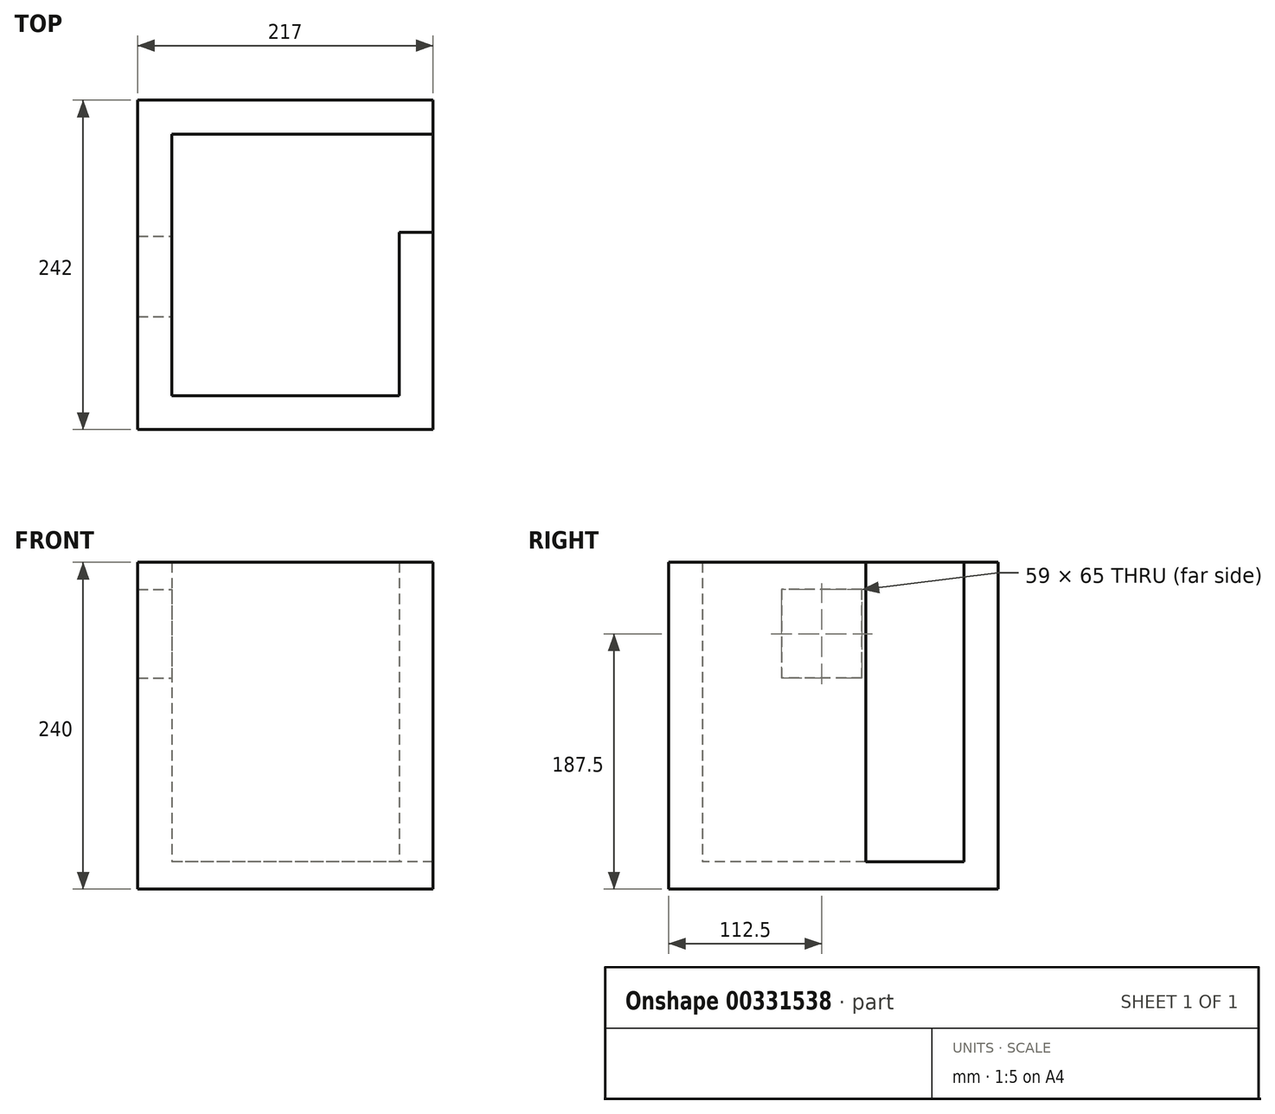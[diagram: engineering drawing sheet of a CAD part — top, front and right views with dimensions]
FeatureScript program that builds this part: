
annotation { "Feature Type Name" : "Feature", "Feature Type Description" : "" }
export const myFeature = defineFeature(function(context is Context, id is Id, definition is map)
    precondition{}
    {
        {
            var Q0;
            Q0=qCreatedBy(makeId("Top.planeOp"),FACE);
            var sketch = newSketch(context, id + "F0", { "sketchPlane" : qUnion([Q0])});
            skLineSegment(sketch, "E0", {"start": v(1313, 440) * mm, "end": v(1313, 406) * mm});
            skLineSegment(sketch, "E1", {"start": v(1313, -267) * mm, "end": v(1313, -301) * mm});
            skLineSegment(sketch, "E2", {"start": v(1313, -301) * mm, "end": v(647, -301) * mm});
            skLineSegment(sketch, "E3", {"start": v(1279, -267) * mm, "end": v(647, -267) * mm});
            skLineSegment(sketch, "E4", {"start": v(1279, 406) * mm, "end": v(688, 406) * mm});
            skLineSegment(sketch, "E5", {"start": v(688, 406) * mm, "end": v(688, -75) * mm});
            skLineSegment(sketch, "E6", {"start": v(688, -75) * mm, "end": v(413, -75) * mm});
            skLineSegment(sketch, "E7", {"start": v(647, -301) * mm, "end": v(647, -267) * mm});
            skLineSegment(sketch, "E8", {"start": v(536, -301) * mm, "end": v(536, -267) * mm});
            skLineSegment(sketch, "E9", {"start": v(536, -267) * mm, "end": v(328, -267) * mm});
            skLineSegment(sketch, "E10", {"start": v(328, -267) * mm, "end": v(328, -407) * mm});
            skLineSegment(sketch, "E11", {"start": v(328, -407) * mm, "end": v(-40, -407) * mm});
            skLineSegment(sketch, "E12", {"start": v(-40, -407) * mm, "end": v(-40, -188) * mm});
            skLineSegment(sketch, "E13", {"start": v(-40, -188) * mm, "end": v(-105, -188) * mm});
            skLineSegment(sketch, "E14", {"start": v(536, -301) * mm, "end": v(362, -301) * mm});
            skLineSegment(sketch, "E15", {"start": v(362, -301) * mm, "end": v(362, -440) * mm});
            skLineSegment(sketch, "E16", {"start": v(-60, -407) * mm, "end": v(-60, -215) * mm});
            skLineSegment(sketch, "E17", {"start": v(-60, -215) * mm, "end": v(-105, -215) * mm});
            skLineSegment(sketch, "E18", {"start": v(-105, -188) * mm, "end": v(-105, -215) * mm});
            skLineSegment(sketch, "E19", {"start": v(-60, -407) * mm, "end": v(-282, -407) * mm});
            skLineSegment(sketch, "E20", {"start": v(-282, -407) * mm, "end": v(-282, -287) * mm});
            skLineSegment(sketch, "E21", {"start": v(-282, -287) * mm, "end": v(-330, -287) * mm});
            skLineSegment(sketch, "E22", {"start": v(-330, -287) * mm, "end": v(-330, -407) * mm});
            skLineSegment(sketch, "E23", {"start": v(-330, -407) * mm, "end": v(-497, -407) * mm});
            skLineSegment(sketch, "E24", {"start": v(-197, -188) * mm, "end": v(-197, -215) * mm});
            skLineSegment(sketch, "E25", {"start": v(-197, -188) * mm, "end": v(-765, -188) * mm});
            skLineSegment(sketch, "E26", {"start": v(-197, -215) * mm, "end": v(-497, -215) * mm});
            skLineSegment(sketch, "E27", {"start": v(-497, -215) * mm, "end": v(-497, -231) * mm});
            skLineSegment(sketch, "E28", {"start": v(-497, -231) * mm, "end": v(-497, -293) * mm});
            skLineSegment(sketch, "E29", {"start": v(-497, -407) * mm, "end": v(-497, -349) * mm});
            skLineSegment(sketch, "E30", {"start": v(413, -75) * mm, "end": v(413, -54) * mm});
            skLineSegment(sketch, "E31", {"start": v(413, -54) * mm, "end": v(667, -54) * mm});
            skLineSegment(sketch, "E32", {"start": v(667, -54) * mm, "end": v(667, 406) * mm});
            skLineSegment(sketch, "E33", {"start": v(667, 406) * mm, "end": v(495, 406) * mm});
            skLineSegment(sketch, "E34", {"start": v(312, 406) * mm, "end": v(391, 406) * mm});
            skLineSegment(sketch, "E35", {"start": v(391, 406) * mm, "end": v(391, 440) * mm});
            skLineSegment(sketch, "E36", {"start": v(495, 406) * mm, "end": v(495, 440) * mm});
            skLineSegment(sketch, "E37", {"start": v(1313, 440) * mm, "end": v(495, 440) * mm});
            skLineSegment(sketch, "E38", {"start": v(312, -75) * mm, "end": v(60, -75) * mm});
            skLineSegment(sketch, "E39", {"start": v(-1279, 406) * mm, "end": v(-1279, 7) * mm});
            skLineSegment(sketch, "E40", {"start": v(-790, 406) * mm, "end": v(-790, 7) * mm});
            skLineSegment(sketch, "E41", {"start": v(-1279, 7) * mm, "end": v(-910, 7) * mm});
            skLineSegment(sketch, "E42", {"start": v(-790, 7) * mm, "end": v(-808, 7) * mm});
            skLineSegment(sketch, "E43", {"start": v(-765, -188) * mm, "end": v(-765, -208) * mm});
            skLineSegment(sketch, "E44", {"start": v(290, 141) * mm, "end": v(290, 406) * mm});
            skLineSegment(sketch, "E45", {"start": v(290, 141) * mm, "end": v(75, 141) * mm});
            skLineSegment(sketch, "E46", {"start": v(75, -46) * mm, "end": v(75, 141) * mm});
            skLineSegment(sketch, "E47", {"start": v(60, -75) * mm, "end": v(60, -46) * mm});
            skLineSegment(sketch, "E48", {"start": v(391, 406) * mm, "end": v(312, 406) * mm});
            skLineSegment(sketch, "E49", {"start": v(-139, 406) * mm, "end": v(-139, 440) * mm});
            skLineSegment(sketch, "E50", {"start": v(-318, 406) * mm, "end": v(-318, 440) * mm});
            skLineSegment(sketch, "E51", {"start": v(-515, 406) * mm, "end": v(-515, 440) * mm});
            skLineSegment(sketch, "E52", {"start": v(-694, 406) * mm, "end": v(-694, 440) * mm});
            skLineSegment(sketch, "E53", {"start": v(-770, 406) * mm, "end": v(-770, 9) * mm});
            skLineSegment(sketch, "E54", {"start": v(-694, 406) * mm, "end": v(-770, 406) * mm});
            skLineSegment(sketch, "E55", {"start": v(75, 406) * mm, "end": v(-139, 406) * mm});
            skLineSegment(sketch, "E56", {"start": v(-318, 406) * mm, "end": v(-515, 406) * mm});
            skLineSegment(sketch, "E57", {"start": v(-318, 440) * mm, "end": v(-515, 440) * mm});
            skLineSegment(sketch, "E58", {"start": v(-770, 9) * mm, "end": v(-754, 9) * mm});
            skLineSegment(sketch, "E59", {"start": v(-677, 9) * mm, "end": v(-659, 9) * mm});
            skLineSegment(sketch, "E60", {"start": v(-659, 9) * mm, "end": v(-659, -5) * mm});
            skLineSegment(sketch, "E61", {"start": v(-659, -5) * mm, "end": v(-659, -46) * mm});
            skLineSegment(sketch, "E62", {"start": v(-659, -46) * mm, "end": v(-60, -46) * mm});
            skLineSegment(sketch, "E63", {"start": v(-60, -75) * mm, "end": v(-60, -46) * mm});
            skLineSegment(sketch, "E64", {"start": v(60, -75) * mm, "end": v(128, -75) * mm});
            skLineSegment(sketch, "E65", {"start": v(60, -46) * mm, "end": v(75, -46) * mm});
            skLineSegment(sketch, "E66", {"start": v(96, -46) * mm, "end": v(290, -46) * mm});
            skLineSegment(sketch, "E67", {"start": v(-60, -75) * mm, "end": v(-677, -75) * mm});
            skLineSegment(sketch, "E68", {"start": v(-677, 9) * mm, "end": v(-677, -75) * mm});
            skLineSegment(sketch, "E69", {"start": v(-754, 9) * mm, "end": v(-754, -13) * mm});
            skLineSegment(sketch, "E70", {"start": v(-808, 7) * mm, "end": v(-808, -13) * mm});
            skLineSegment(sketch, "E71", {"start": v(-808, -13) * mm, "end": v(-754, -13) * mm});
            skLineSegment(sketch, "E72", {"start": v(-910, 7) * mm, "end": v(-910, -29) * mm});
            skLineSegment(sketch, "E73", {"start": v(-1279, -406) * mm, "end": v(-935, -406) * mm});
            skLineSegment(sketch, "E74", {"start": v(-1313, -440) * mm, "end": v(-935, -440) * mm});
            skLineSegment(sketch, "E75", {"start": v(-910, -29) * mm, "end": v(-935, -29) * mm});
            skLineSegment(sketch, "E76", {"start": v(-935, -13) * mm, "end": v(-1279, -13) * mm});
            skLineSegment(sketch, "E77", {"start": v(-910, -132) * mm, "end": v(-935, -132) * mm});
            skLineSegment(sketch, "E78", {"start": v(-910, -29) * mm, "end": v(-910, -13) * mm});
            skLineSegment(sketch, "E79", {"start": v(-935, -406) * mm, "end": v(-935, -132) * mm});
            skLineSegment(sketch, "E80", {"start": v(-935, -29) * mm, "end": v(-935, -13) * mm});
            skLineSegment(sketch, "E81", {"start": v(-877, -208) * mm, "end": v(-877, -188) * mm});
            skLineSegment(sketch, "E82", {"start": v(-910, -132) * mm, "end": v(-910, -188) * mm});
            skLineSegment(sketch, "E83", {"start": v(-877, -188) * mm, "end": v(-910, -188) * mm});
            skLineSegment(sketch, "E84", {"start": v(-877, -208) * mm, "end": v(-904, -208) * mm});
            skLineSegment(sketch, "E85", {"start": v(-904, -208) * mm, "end": v(-904, -406) * mm});
            skLineSegment(sketch, "E86", {"start": v(-904, -406) * mm, "end": v(-648, -406) * mm});
            skLineSegment(sketch, "E87", {"start": v(-765, -208) * mm, "end": v(-648, -208) * mm});
            skLineSegment(sketch, "E88", {"start": v(-648, -208) * mm, "end": v(-648, -273) * mm});
            skLineSegment(sketch, "E89", {"start": v(-648, -406) * mm, "end": v(-648, -343) * mm});
            skLineSegment(sketch, "E90", {"start": v(-935, -440) * mm, "end": v(362, -440) * mm});
            skLineSegment(sketch, "E91", {"start": v(151, 406) * mm, "end": v(151, 440) * mm});
            skLineSegment(sketch, "E92", {"start": v(224, 406) * mm, "end": v(224, 440) * mm});
            skLineSegment(sketch, "E93", {"start": v(290, 406) * mm, "end": v(224, 406) * mm});
            skLineSegment(sketch, "E94", {"start": v(151, 406) * mm, "end": v(96, 406) * mm});
            skLineSegment(sketch, "E95", {"start": v(391, 440) * mm, "end": v(224, 440) * mm});
            skLineSegment(sketch, "E96", {"start": v(151, 440) * mm, "end": v(-139, 440) * mm});
            skLineSegment(sketch, "E97", {"start": v(-907, 406) * mm, "end": v(-907, 440) * mm});
            skLineSegment(sketch, "E98", {"start": v(-1085, 406) * mm, "end": v(-1085, 440) * mm});
            skLineSegment(sketch, "E99", {"start": v(-790, 406) * mm, "end": v(-907, 406) * mm});
            skLineSegment(sketch, "E100", {"start": v(-1085, 406) * mm, "end": v(-1279, 406) * mm});
            skLineSegment(sketch, "E101", {"start": v(-694, 440) * mm, "end": v(-907, 440) * mm});
            skLineSegment(sketch, "E102", {"start": v(-1085, 440) * mm, "end": v(-1313, 440) * mm});
            skLineSegment(sketch, "E103", {"start": v(-1279, -118) * mm, "end": v(-1313, -118) * mm});
            skLineSegment(sketch, "E104", {"start": v(-1279, -297) * mm, "end": v(-1313, -297) * mm});
            skLineSegment(sketch, "E105", {"start": v(-1279, -13) * mm, "end": v(-1279, -118) * mm});
            skLineSegment(sketch, "E106", {"start": v(-1279, -297) * mm, "end": v(-1279, -406) * mm});
            skLineSegment(sketch, "E107", {"start": v(-1313, 440) * mm, "end": v(-1313, -118) * mm});
            skLineSegment(sketch, "E108", {"start": v(-1313, -297) * mm, "end": v(-1313, -440) * mm});
            skLineSegment(sketch, "E109", {"start": v(-648, -273) * mm, "end": v(-630, -273) * mm});
            skLineSegment(sketch, "E110", {"start": v(-648, -343) * mm, "end": v(-630, -343) * mm});
            skLineSegment(sketch, "E111", {"start": v(-515, -349) * mm, "end": v(-497, -349) * mm});
            skLineSegment(sketch, "E112", {"start": v(-515, -293) * mm, "end": v(-497, -293) * mm});
            skLineSegment(sketch, "E113", {"start": v(-515, -349) * mm, "end": v(-515, -406) * mm});
            skLineSegment(sketch, "E114", {"start": v(-630, -343) * mm, "end": v(-630, -406) * mm});
            skLineSegment(sketch, "E115", {"start": v(-630, -406) * mm, "end": v(-515, -406) * mm});
            skLineSegment(sketch, "E116", {"start": v(-630, -273) * mm, "end": v(-630, -206) * mm});
            skLineSegment(sketch, "E117", {"start": v(-630, -206) * mm, "end": v(-515, -206) * mm});
            skLineSegment(sketch, "E118", {"start": v(-515, -293) * mm, "end": v(-515, -206) * mm});
            skLineSegment(sketch, "E119", {"start": v(290, 43) * mm, "end": v(312, 43) * mm});
            skLineSegment(sketch, "E120", {"start": v(290, 124) * mm, "end": v(312, 124) * mm});
            skLineSegment(sketch, "E121", {"start": v(312, -75) * mm, "end": v(312, 43) * mm});
            skLineSegment(sketch, "E122", {"start": v(312, 124) * mm, "end": v(312, 406) * mm});
            skLineSegment(sketch, "E123", {"start": v(290, -46) * mm, "end": v(290, 43) * mm});
            skLineSegment(sketch, "E124", {"start": v(96, 222) * mm, "end": v(75, 222) * mm});
            skLineSegment(sketch, "E125", {"start": v(96, 222) * mm, "end": v(96, 406) * mm});
            skLineSegment(sketch, "E126", {"start": v(75, 222) * mm, "end": v(75, 406) * mm});
            skLineSegment(sketch, "E127", {"start": v(96, -46) * mm, "end": v(96, 124) * mm});
            skLineSegment(sketch, "E128", {"start": v(290, 124) * mm, "end": v(96, 124) * mm});
            skLineSegment(sketch, "E129", {"start": v(1279, -219) * mm, "end": v(1313, -219) * mm});
            skLineSegment(sketch, "E130", {"start": v(1279, -26) * mm, "end": v(1313, -26) * mm});
            skLineSegment(sketch, "E131", {"start": v(1279, 46) * mm, "end": v(1313, 46) * mm});
            skLineSegment(sketch, "E132", {"start": v(1279, 239) * mm, "end": v(1313, 239) * mm});
            skLineSegment(sketch, "E133", {"start": v(1313, 406) * mm, "end": v(1313, 239) * mm});
            skLineSegment(sketch, "E134", {"start": v(1279, 406) * mm, "end": v(1279, 239) * mm});
            skLineSegment(sketch, "E135", {"start": v(1313, 46) * mm, "end": v(1313, -26) * mm});
            skLineSegment(sketch, "E136", {"start": v(1313, -219) * mm, "end": v(1313, -267) * mm});
            skLineSegment(sketch, "E137", {"start": v(1279, 46) * mm, "end": v(1279, -26) * mm});
            skLineSegment(sketch, "E138", {"start": v(1279, -219) * mm, "end": v(1279, -267) * mm});
            skLineSegment(sketch, "E139", {"start": v(1313, -301) * mm, "end": v(1313, 440) * mm});
            skLineSegment(sketch, "E140", {"start": v(1313, -301) * mm, "end": v(362, -301) * mm});
            skLineSegment(sketch, "E141", {"start": v(362, -440) * mm, "end": v(-1313, -440) * mm});
            skLineSegment(sketch, "E142", {"start": v(-1313, 440) * mm, "end": v(-1313, -440) * mm});
            skLineSegment(sketch, "E143", {"start": v(-1313, 440) * mm, "end": v(1313, 440) * mm});
            skLineSegment(sketch, "E144", {"start": v(-321.5, -37.21) * mm, "end": v(-321.5, 162.79) * mm});
            skLineSegment(sketch, "E145", {"start": v(-321.5, -37.21) * mm, "end": v(-511.5, -37.21) * mm});
            skLineSegment(sketch, "E146", {"start": v(-321.5, 162.79) * mm, "end": v(-511.5, 162.79) * mm});
            skLineSegment(sketch, "E147", {"start": v(-511.5, -37.21) * mm, "end": v(-511.5, 162.79) * mm});
            skLineSegment(sketch, "E148", {"start": v(-321.5, -29.2) * mm, "end": v(-511.5, -29.2) * mm});
            skLineSegment(sketch, "E149", {"start": v(-499.08, -21.75) * mm, "end": v(-430.85, -21.75) * mm});
            skLineSegment(sketch, "E150", {"start": v(-430.85, -21.75) * mm, "end": v(-430.85, 2.94) * mm});
            skLineSegment(sketch, "E151", {"start": v(-430.85, 2.94) * mm, "end": v(-499.08, 2.94) * mm});
            skLineSegment(sketch, "E152", {"start": v(-499.08, 2.94) * mm, "end": v(-499.08, -21.75) * mm});
            skLineSegment(sketch, "E153", {"start": v(-333.92, -21.75) * mm, "end": v(-402.15, -21.75) * mm});
            skLineSegment(sketch, "E154", {"start": v(-402.15, -21.75) * mm, "end": v(-402.15, 2.94) * mm});
            skLineSegment(sketch, "E155", {"start": v(-402.15, 2.94) * mm, "end": v(-333.92, 2.94) * mm});
            skLineSegment(sketch, "E156", {"start": v(-333.92, 2.94) * mm, "end": v(-333.92, -21.75) * mm});
            skLineSegment(sketch, "E157", {"start": v(-321.5, 13.1) * mm, "end": v(-416.5, 13.1) * mm});
            skLineSegment(sketch, "E158", {"start": v(-511.5, 36.6) * mm, "end": v(-491.94, 63.04) * mm});
            skLineSegment(sketch, "E159", {"start": v(-491.94, 63.04) * mm, "end": v(-416.5, 13.1) * mm});
            skLineSegment(sketch, "E160", {"start": v(-416.5, 13.1) * mm, "end": v(-511.5, 36.6) * mm});
            skLineSegment(sketch, "E161", {"start": v(-321.5, 159.23) * mm, "end": v(-511.5, 159.23) * mm});
            skLineSegment(sketch, "E162", {"start": v(-552.43, 3.31) * mm, "end": v(-520.43, 3.31) * mm});
            skLineSegment(sketch, "E163", {"start": v(-552.43, 3.31) * mm, "end": v(-552.43, -36.7) * mm});
            skLineSegment(sketch, "E164", {"start": v(-520.43, 3.31) * mm, "end": v(-520.43, -36.7) * mm});
            skLineSegment(sketch, "E165", {"start": v(-552.43, -36.7) * mm, "end": v(-520.43, -36.7) * mm});
            skLineSegment(sketch, "E166", {"start": v(-552.43, -6.69) * mm, "end": v(-520.43, -6.69) * mm});
            skLineSegment(sketch, "E167", {"start": v(-552.43, -3.69) * mm, "end": v(-520.43, -3.69) * mm});
            skLineSegment(sketch, "E168", {"start": v(-552.43, -0.69) * mm, "end": v(-520.43, -0.69) * mm});
            skLineSegment(sketch, "E169", {"start": v(-552.43, 2.31) * mm, "end": v(-520.43, 2.31) * mm});
            skLineSegment(sketch, "E170", {"start": v(-280.57, 3.31) * mm, "end": v(-312.57, 3.31) * mm});
            skLineSegment(sketch, "E171", {"start": v(-280.57, 3.31) * mm, "end": v(-280.57, -36.7) * mm});
            skLineSegment(sketch, "E172", {"start": v(-312.57, 3.31) * mm, "end": v(-312.57, -36.7) * mm});
            skLineSegment(sketch, "E173", {"start": v(-280.57, -36.7) * mm, "end": v(-312.57, -36.7) * mm});
            skLineSegment(sketch, "E174", {"start": v(-280.57, -6.69) * mm, "end": v(-312.57, -6.69) * mm});
            skLineSegment(sketch, "E175", {"start": v(-280.57, -3.69) * mm, "end": v(-312.57, -3.69) * mm});
            skLineSegment(sketch, "E176", {"start": v(-280.57, -0.69) * mm, "end": v(-312.57, -0.69) * mm});
            skLineSegment(sketch, "E177", {"start": v(-280.57, 2.31) * mm, "end": v(-312.57, 2.31) * mm});
            skLineSegment(sketch, "E178", {"start": v(-765, 395.6) * mm, "end": v(-765, 20.6) * mm});
            skLineSegment(sketch, "E179", {"start": v(-765, 395.6) * mm, "end": v(-705, 395.6) * mm});
            skLineSegment(sketch, "E180", {"start": v(-705, 395.6) * mm, "end": v(-705, 20.6) * mm});
            skLineSegment(sketch, "E181", {"start": v(-765, 20.6) * mm, "end": v(-705, 20.6) * mm});
            skLineSegment(sketch, "E182", {"start": v(-705, 395.6) * mm, "end": v(-700, 395.6) * mm});
            skLineSegment(sketch, "E183", {"start": v(-700, 395.6) * mm, "end": v(-700, 20.6) * mm});
            skLineSegment(sketch, "E184", {"start": v(-705, 20.6) * mm, "end": v(-700, 20.6) * mm});
            skLineSegment(sketch, "E185", {"start": v(-705, 114.35) * mm, "end": v(-700, 114.35) * mm});
            skLineSegment(sketch, "E186", {"start": v(-705, 301.85) * mm, "end": v(-700, 301.85) * mm});
            skLineSegment(sketch, "E187", {"start": v(-705, 208.1) * mm, "end": v(-700, 208.1) * mm});
            skLineSegment(sketch, "E188", {"start": v(-705, 348.73) * mm, "end": v(-700, 348.73) * mm});
            skLineSegment(sketch, "E189", {"start": v(-705, 67.47) * mm, "end": v(-700, 67.47) * mm});
            skSolve(sketch);
        }
        {
            var Q0;
            Q0=makeQuery(id+"F0.imprint","IMPRINT",FACE,{"disambiguationData":[TD([[makeQuery(id+"F0.imprint","IMPRINT",EDGE,{"derivedFrom":sQuery(id+"F0.wireOp",EDGE,"E3")}),-1.0]])]});
            var sketch = newSketch(context, id + "F1", { "sketchPlane" : qUnion([Q0])});
            skLineSegment(sketch, "E190.0", {"start": v(-497, -231) * mm, "end": v(-497, -293) * mm});
            skLineSegment(sketch, "E191.0", {"start": v(-330, -215) * mm, "end": v(-497, -215) * mm});
            skLineSegment(sketch, "E192.0", {"start": v(-330, -287) * mm, "end": v(-330, -407) * mm});
            skLineSegment(sketch, "E193.0", {"start": v(-330, -407) * mm, "end": v(-497, -407) * mm});
            skLineSegment(sketch, "E194", {"start": v(-330, -287) * mm, "end": v(-330, -215) * mm});
            skLineSegment(sketch, "E195", {"start": v(-497, -215) * mm, "end": v(-497, -231) * mm});
            skLineSegment(sketch, "E196", {"start": v(-497, -293) * mm, "end": v(-497, -407) * mm});
            skPoint(sketch, "E197.orphan", {"position": v(-197, -215) * mm});
            skSolve(sketch);
        }
        {
            var Q0;
            Q0 = qSketchRegion(id + "F1", true);
            extrude(context, id + "F2", {"entities" : qUnion([Q0]), "depth" : 20 * mm});
        }
        {
            var Q0;
            Q0=makeQuery(id+"F0.imprint","IMPRINT",FACE,{"disambiguationData":[TD([[makeQuery(id+"F0.imprint","IMPRINT",EDGE,{"derivedFrom":sQuery(id+"F0.wireOp",EDGE,"E3")}),-1.0]])]});
            var sketch = newSketch(context, id + "F3", { "sketchPlane" : qUnion([Q0])});
            skLineSegment(sketch, "E198.0", {"start": v(-522, -190) * mm, "end": v(-522, -432) * mm});
            skLineSegment(sketch, "E198.1", {"start": v(-305, -190) * mm, "end": v(-522, -190) * mm});
            skLineSegment(sketch, "E198.2", {"start": v(-305, -432) * mm, "end": v(-305, -190) * mm});
            skLineSegment(sketch, "E198.3", {"start": v(-522, -432) * mm, "end": v(-305, -432) * mm});
            skLineSegment(sketch, "E199.0.0", {"start": v(-497, -215) * mm, "end": v(-497, -407) * mm});
            skLineSegment(sketch, "E199.0.1", {"start": v(-497, -407) * mm, "end": v(-330, -407) * mm});
            skLineSegment(sketch, "E199.0.2", {"start": v(-330, -407) * mm, "end": v(-330, -215) * mm});
            skLineSegment(sketch, "E199.0.3", {"start": v(-330, -215) * mm, "end": v(-497, -215) * mm});
            skSolve(sketch);
        }
        {
            var Q0;
            Q0 = qSketchRegion(id + "F3", true);
            extrude(context, id + "F4", {"entities" : qUnion([Q0]), "operationType" : NewBodyOperationType.ADD, "depth" : (220 + 20) * mm});
        }
        {
            var Q0;
            Q0=makeQuery(id+"F2.opExtrude","CAP_FACE",FACE,{"disambiguationData":[OSD([sQuery(id+"F1.wireOp",EDGE,"E190.0"),sQuery(id+"F1.wireOp",EDGE,"E191.0"),sQuery(id+"F1.wireOp",EDGE,"E192.0"),sQuery(id+"F1.wireOp",EDGE,"E193.0"),sQuery(id+"F1.wireOp",EDGE,"E194"),sQuery(id+"F1.wireOp",EDGE,"E195"),sQuery(id+"F1.wireOp",EDGE,"E196")])],"isStart":false});
            var sketch = newSketch(context, id + "F5", { "sketchPlane" : qUnion([Q0])});
            skLineSegment(sketch, "E200.0", {"start": v(-282, -287) * mm, "end": v(-330, -287) * mm});
            skLineSegment(sketch, "E201.0", {"start": v(-282, -215) * mm, "end": v(-330, -215) * mm});
            skLineSegment(sketch, "E202", {"start": v(-330, -287) * mm, "end": v(-330, -215) * mm});
            skLineSegment(sketch, "E203", {"start": v(-282, -287) * mm, "end": v(-282, -215) * mm});
            skPoint(sketch, "E204.orphan", {"position": v(-197, -215) * mm});
            skPoint(sketch, "E205.orphan", {"position": v(-497, -215) * mm});
            skSolve(sketch);
        }
        {
            var Q0;
            Q0 = qSketchRegion(id + "F5", true);
            extrude(context, id + "F6", {"entities" : qUnion([Q0]), "operationType" : NewBodyOperationType.REMOVE, "depth" : 250 * mm});
        }
        {
            var Q0;
            Q0=makeQuery(id+"F4.opExtrude","SWEPT_FACE",FACE,{"disambiguationData":[OSD([sQuery(id+"F3.wireOp",EDGE,"E199.0.0")])]});
            var sketch = newSketch(context, id + "F7", { "sketchPlane" : qUnion([Q0])});
            skLineSegment(sketch, "E206.0", {"start": v(-407, 0) * mm, "end": v(-349, 0) * mm});
            skLineSegment(sketch, "E207", {"start": v(-270, 220) * mm, "end": v(-349, 220) * mm});
            skLineSegment(sketch, "E208", {"start": v(-349, 220) * mm, "end": v(-349, 135) * mm});
            skLineSegment(sketch, "E209", {"start": v(-349, 135) * mm, "end": v(-270, 135) * mm});
            skLineSegment(sketch, "E210", {"start": v(-270, 135) * mm, "end": v(-270, 220) * mm});
            skSolve(sketch);
        }
        {
            var Q0;
            Q0 = qSketchRegion(id + "F7", true);
            extrude(context, id + "F8", {"entities" : qUnion([Q0]), "operationType" : NewBodyOperationType.REMOVE, "oppositeDirection" : true, "depth" : 25 * mm});
        }
        {
            var Q0;
            Q0=makeQuery(id+"F4.opExtrude","SWEPT_FACE",FACE,{"disambiguationData":[OSD([sQuery(id+"F3.wireOp",EDGE,"E199.0.0")])]});
            var sketch = newSketch(context, id + "F9", { "sketchPlane" : qUnion([Q0])});
            skLineSegment(sketch, "E211", {"start": v(-270, 220) * mm, "end": v(-290, 220) * mm});
            skLineSegment(sketch, "E212.0", {"start": v(-270, 135) * mm, "end": v(-270, 220) * mm});
            skLineSegment(sketch, "E213.0", {"start": v(-349, 135) * mm, "end": v(-270, 135) * mm});
            skLineSegment(sketch, "E214", {"start": v(-290, 220) * mm, "end": v(-290, 155) * mm});
            skLineSegment(sketch, "E215", {"start": v(-349, 135) * mm, "end": v(-349, 155) * mm});
            skLineSegment(sketch, "E216", {"start": v(-349, 155) * mm, "end": v(-290, 155) * mm});
            skSolve(sketch);
        }
        {
            var Q0;
            Q0 = qSketchRegion(id + "F9", true);
            var Q1;
            Q1=makeQuery(id+"F4.opExtrude","SWEPT_FACE",FACE,{"disambiguationData":[OSD([sQuery(id+"F3.wireOp",EDGE,"E198.0")])]});
            extrude(context, id + "F10", {"entities" : qUnion([Q0]), "operationType" : NewBodyOperationType.ADD, "endBound" : BoundingType.UP_TO_SURFACE, "oppositeDirection" : true, "endBoundEntityFace" : qUnion([Q1]), "depth" : 25 * mm});
        }
    });
